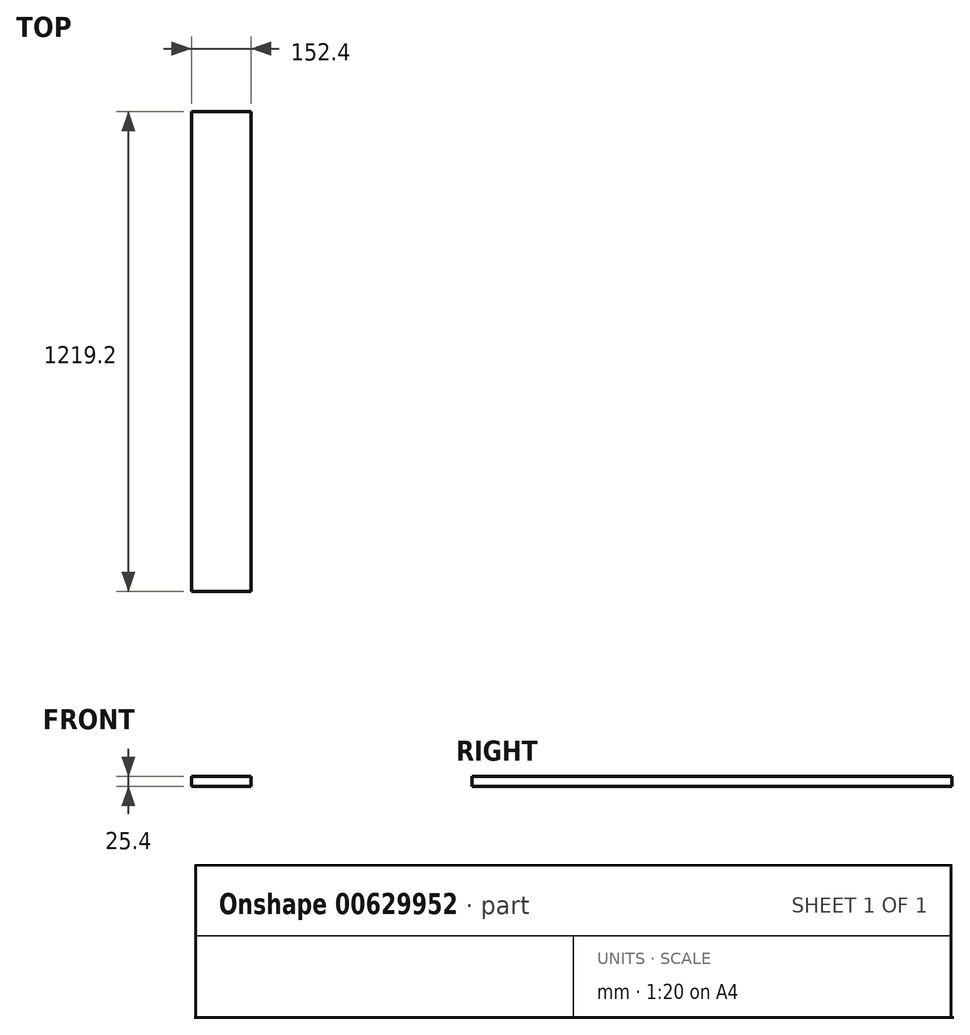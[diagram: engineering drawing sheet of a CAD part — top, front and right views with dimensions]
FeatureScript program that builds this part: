
annotation { "Feature Type Name" : "Feature", "Feature Type Description" : "" }
export const myFeature = defineFeature(function(context is Context, id is Id, definition is map)
    precondition{}
    {
        {
            var Q0;
            Q0=qCreatedBy(makeId("Front.planeOp"),FACE);
            var sketch = newSketch(context, id + "F0", { "sketchPlane" : qUnion([Q0])});
            skLineSegment(sketch, "E0.bottom", {"start": v(-75.05, 4.16) * mm, "end": v(77.35, 4.16) * mm});
            skLineSegment(sketch, "E0.top", {"start": v(-75.05, -21.24) * mm, "end": v(77.35, -21.24) * mm});
            skLineSegment(sketch, "E0.left", {"start": v(-75.05, 4.16) * mm, "end": v(-75.05, -21.24) * mm});
            skLineSegment(sketch, "E0.right", {"start": v(77.35, 4.16) * mm, "end": v(77.35, -21.24) * mm});
            skSolve(sketch);
        }
        {
            var Q0;
            Q0 = qSketchRegion(id + "F0", true);
            extrude(context, id + "F1", {"entities" : qUnion([Q0]), "depth" : 1219.2 * mm, "offsetDistance" : 25.4 * mm});
        }
    });
